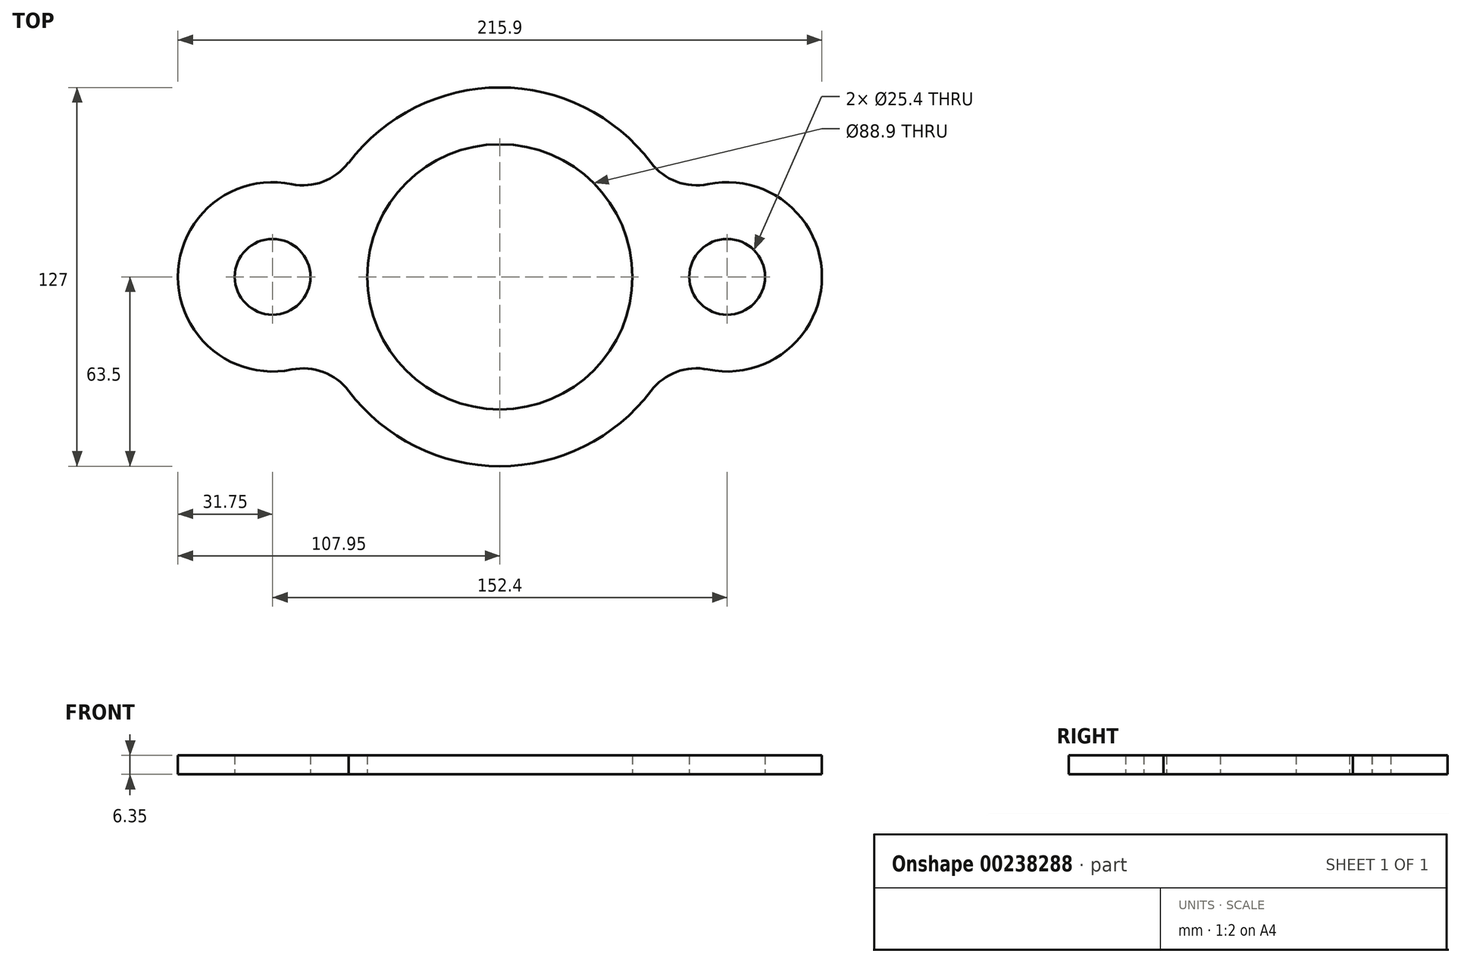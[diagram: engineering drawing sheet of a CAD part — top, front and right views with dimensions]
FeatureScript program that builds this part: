
annotation { "Feature Type Name" : "Feature", "Feature Type Description" : "" }
export const myFeature = defineFeature(function(context is Context, id is Id, definition is map)
    precondition{}
    {
        {
            var Q0;
            Q0=qCreatedBy(makeId("Top.planeOp"),FACE);
            var sketch = newSketch(context, id + "F0", { "sketchPlane" : qUnion([Q0])});
            skCircle(sketch, "E0", {"center": v(0, 0) * mm, "radius": 44.45 * mm});
            skCircle(sketch, "E1", {"center": v(-76.2, 0) * mm, "radius": 12.7 * mm});
            skCircle(sketch, "E2", {"center": v(76.2, 0) * mm, "radius": 12.7 * mm});
            skLineSegment(sketch, "E3", {"start": v(-57.94, -25.98) * mm, "end": v(-57.94, -25.98) * mm});
            skLineSegment(sketch, "E4", {"start": v(57.94, -25.98) * mm, "end": v(57.94, -25.98) * mm});
            skArc(sketch, "E5", {"start": v(-69.78, 31.1) * mm, "mid": v(-107.95, -0.01) * mm, "end": v(-69.76, -31.1) * mm});
            skArc(sketch, "E6", {"start": v(-69.93, 31.13) * mm, "mid": v(-59.34, 31.9) * mm, "end": v(-50.83, 38.25) * mm});
            skLineSegment(sketch, "E7.trimOffspring", {"start": v(-50.74, 38.19) * mm, "end": v(-50.83, 38.25) * mm});
            skArc(sketch, "E8", {"start": v(50.68, 38.26) * mm, "mid": v(59.17, 31.91) * mm, "end": v(69.75, 31.09) * mm});
            skArc(sketch, "E9", {"start": v(50.68, 38.26) * mm, "mid": v(-0.05, 63.5) * mm, "end": v(-50.74, 38.19) * mm});
            skArc(sketch, "E10", {"start": v(-50.72, -38.26) * mm, "mid": v(-59.2, -31.91) * mm, "end": v(-69.76, -31.09) * mm});
            skArc(sketch, "E11", {"start": v(-50.7, -38.24) * mm, "mid": v(-0.01, -63.5) * mm, "end": v(50.68, -38.26) * mm});
            skArc(sketch, "E12", {"start": v(-69.76, -31.1) * mm, "mid": v(-69.76, -31.1) * mm, "end": v(-69.76, -31.09) * mm});
            skLineSegment(sketch, "E13.trimOffspring", {"start": v(-50.7, -38.24) * mm, "end": v(-50.72, -38.26) * mm});
            skArc(sketch, "E14", {"start": v(69.75, -31.09) * mm, "mid": v(59.17, -31.91) * mm, "end": v(50.68, -38.26) * mm});
            skArc(sketch, "E15", {"start": v(69.75, -31.09) * mm, "mid": v(107.95, 0.12) * mm, "end": v(69.52, 31.04) * mm});
            skSolve(sketch);
        }
        {
            var Q0;
            Q0 = qSketchRegion(id + "F0", true);
            extrude(context, id + "F1", {"entities" : qUnion([Q0]), "depth" : 6.35 * mm});
        }
    });
